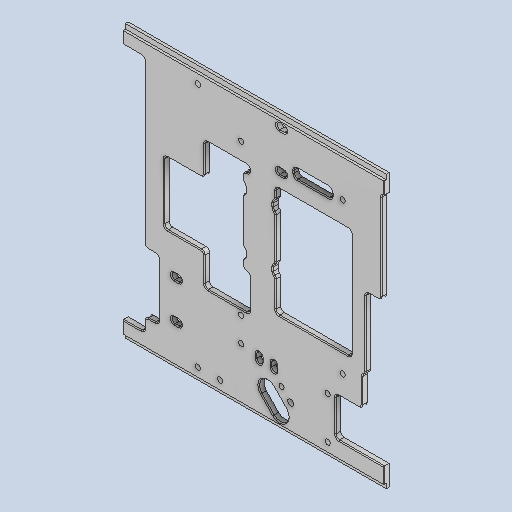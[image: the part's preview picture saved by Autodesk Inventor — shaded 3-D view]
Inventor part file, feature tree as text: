
AUTODESK INVENTOR PART (.ipt)
format: ipt  version: 2024.2 (Build 282272000, 272)  size: 785,920 bytes
history: native  units: mm
features: extrude x21, reference x18, other x9, fillet x6, thicken_offset x6, projected_geometry x3, sketch x3, chamfer x1
ambient origin geometry x8: Origin, YZ Plane, XZ Plane, XY Plane, X Axis, Y Axis, Z Axis, Center Point
bodies: Solid1 (feature_tree)
feature tree (67):
  extrude  "Extrusion1"  Depth=150.0mm
  extrude  "Extrusion2"  Depth=10.0mm
  extrude  "Extrusion3"  Depth=6.0mm
  extrude  "Extrusion4"  TaperAngle=0.0deg  [1 undecoded]
  extrude  "Extrusion5"  Depth=6.0mm
  extrude  "Extrusion6"  Depth=6.0mm
  extrude  "Extrusion7"  Depth=6.0mm
  extrude  "Extrusion8"  Depth=6.0mm
  extrude  "Extrusion9"  Depth=6.0mm
  extrude  "Extrusion10"  Depth=6.0mm
  extrude  "Extrusion11"  Depth=19.598mm
  extrude  "Extrusion12"  TaperAngle=0.0deg  [1 undecoded]
  extrude  "Extrusion13"  Depth=6.0mm
  extrude  "Extrusion14"  Depth=6.0mm
  fillet  "Fillet1"  Radius=34.0mm
  fillet  "Fillet2"  Radius=10.0mm
  fillet  "Fillet3"  Radius=4.0mm
  extrude  "Extrusion15"  Depth=6.0mm
  extrude  "Extrusion16"  Depth=47.0mm
  fillet  "Fillet4"  Radius=30.0mm
  extrude  "Extrusion17"  Depth=6.0mm
  thicken_offset  "Thicken1"
  thicken_offset  "Thicken2"
  thicken_offset  "Thicken3"
  thicken_offset  "Thicken4"
  extrude  "Extrusion18"  Depth=22.0mm
  thicken_offset  "Thicken5"
  thicken_offset  "Thicken6"
  extrude  "Extrusion19"  Depth=5.5mm
  fillet  "Fillet5"  Radius=10.0mm
  extrude  "Extrusion20"  Depth=5.0mm TaperAngle=0.0deg
  fillet  "Fillet6"  Radius=3.0mm
  extrude  "Extrusion21"  Depth=3.0mm
  chamfer  "Chamfer1"  Distance=1.2mm
  projected_geometry  "Projected Loop1"
  reference  "Reference1"
  reference  "Reference2"
  reference  "Reference3"
  reference  "Reference4"
  reference  "Reference7"
  reference  "Reference8"
  reference  "Reference9"
  reference  "Reference10"
  reference  "Reference11"
  reference  "Reference12"
  projected_geometry  "Projected Loop2"
  reference  "Reference13"
  reference  "Reference14"
  reference  "Reference15"
  reference  "Reference16"
  reference  "Reference17"
  reference  "Reference18"
  reference  "Reference19"
  sketch  "Sketch12"  dims[d0=150.0mm d1=156.0mm]
  reference  "Reference20"
  sketch  "Sketch16"  dims[d2=1.8mm d3=0.0mm d4=10.0mm]
  projected_geometry  "Projected Loop3"
  sketch  "Sketch21"  dims[d5=10.0mm d6=13.0mm d7=0.0mm d8=0.0mm d9=14.903711mm d10=14.90369mm d11=33.425867mm d12=5.537mm d13=8.898mm d14=23.737mm d15=19.598mm d16=0.0mm d17=0.0mm d18=49.0mm d19=77.0mm d20=34.0mm d22=10.0mm d23=0.0mm d24=4.0mm d25=69.0mm d26=47.0mm d27=30.0mm d28=27.0mm d30=22.0mm d31=5.5mm d32=10.0mm d33=0.0mm d34=5.0mm d35=0.0mm d36=3.0mm d37=3.0mm d38=1.2mm d39=0.0mm d40=53.0mm d41=67.0mm d42=23.0mm d43=0.0mm d44=0.0mm d45=0.0mm d46=0.0mm d47=10.0mm d48=10.0mm d50=2.0mm d51=0.0mm d52=0.0mm d53=53.0mm d54=12.0mm d55=22.0mm d56=0.0mm d57=0.0mm d58=36.0mm d59=8.0mm d60=0.0mm d61=0.0mm d62=34.0mm d63=8.0mm d64=0.0mm d65=0.0mm d66=6.0mm d67=3.5mm d68=3.5mm d70=6.0mm d71=59.0mm d72=6.0mm d73=3.5mm d74=3.5mm d75=18.0mm d77=10.0mm d78=0.0mm d79=0.0mm d80=2.0mm d81=1.75mm d82=2.0mm d83=10.0mm d84=10.0mm d85=12.75mm d86=63.5mm d87=0.0mm d88=0.0mm d89=3.0mm d90=3.0mm d91=3.0mm d94=3.0mm d95=3.0mm d96=3.0mm d97=3.0mm d98=3.0mm d99=3.0mm d100=3.0mm d101=0.0mm d102=0.0mm d103=2.0mm d104=18.0mm d105=2.0mm d106=0.5mm d107=0.5mm d108=0.0mm d109=0.0mm d110=0.25mm d111=0.25mm d112=0.25mm d113=0.25mm d114=0.25mm d115=0.25mm d116=0.25mm d117=0.25mm d118=15.0mm d119=34.0mm d120=6.25mm d121=6.0mm d122=3.5mm d125=10.0mm d126=0.0mm d127=5.0mm d128=90.0deg d130=10.0mm d131=5.0mm d132=3.75mm d133=3.75mm d134=3.0mm d135=0.05mm d136=0.05mm d137=0.05mm d138=0.05mm d139=9.0mm d140=6.0mm d141=4.0mm d142=4.0mm d143=4.0mm d144=0.0mm d145=0.0mm d146=2.0mm d147=18.0mm d148=1.5mm d149=1.5mm d150=6.0mm d151=6.0mm d152=3.650067mm d153=3.650067mm d154=0.0mm d155=0.0mm d156=2.0mm d157=1.75mm d158=1.75mm d159=2.5mm d160=2.5mm d161=5.0mm d162=0.0mm d163=35.0mm d164=18.0mm d165=10.0mm d166=0.0mm d167=0.5mm d168=2.0mm d169=45.0deg d171=22.0mm d172=10.0mm d174=6.0mm d175=6.0mm]
  other  "<userpath>\Google Drive\Unicorn 2020\CAD\Assembly.iam"
  other  "Assembly.iam"
  other  "Jetson_Nano_Dev_Kit_3D_b01:1"
  other  "682-13450_PORG_ME_THER_ASSY:1"
  other  "USB_MAIN_PCB:1"
  other  "IO_HEADER_PCB_ASS:1"
  other  "IO_HEADER_PCB:1"
  other  "84161000_ABD-1600_Back:1"
  other  "DI 1600:1"
note: 2 required parameter values undecoded (feature->parameter linkage not recoverable at this tier; creation-order binding heuristic only, values carry confidence <= 0.55)
